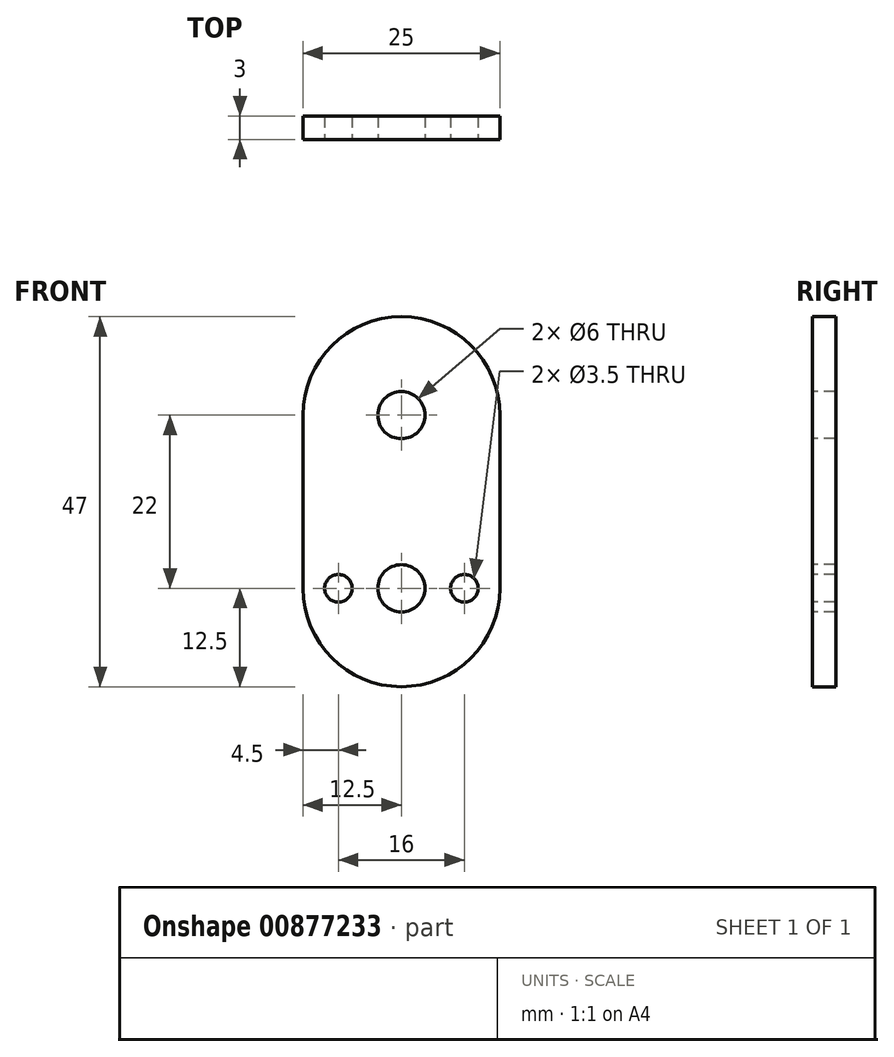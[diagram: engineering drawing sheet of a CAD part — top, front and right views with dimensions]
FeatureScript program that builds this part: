
annotation { "Feature Type Name" : "Feature", "Feature Type Description" : "" }
export const myFeature = defineFeature(function(context is Context, id is Id, definition is map)
    precondition{}
    {
        {
            var Q0;
            Q0=qCreatedBy(makeId("Front.planeOp"),FACE);
            var sketch = newSketch(context, id + "F0", { "sketchPlane" : qUnion([Q0])});
            skCircle(sketch, "E0", {"center": v(0, 11) * mm, "radius": 12.5 * mm});
            skLineSegment(sketch, "E1", {"start": v(-12.5, 11) * mm, "end": v(-12.5, 0) * mm});
            skLineSegment(sketch, "E2", {"start": v(12.5, 11) * mm, "end": v(12.5, 0) * mm});
            skLineSegment(sketch, "E3", {"start": v(12.5, 0) * mm, "end": v(-12.5, 0) * mm});
            skSolve(sketch);
        }
        {
            var Q0;
            {var subQ0=sQuery(id+"F0.wireOp",EDGE,"E0");var subQ1=makeQuery(id+"F0.imprint","INTERSECT",VERTEX,{"derivedFrom":[subQ0,sQuery(id+"F0.wireOp",EDGE,"E1")]});Q0=makeQuery(id+"F0.imprint","IMPRINT",FACE,{"disambiguationData":[TD([[makeQuery(id+"F0.imprint","IMPRINT",EDGE,{"disambiguationData":[TD([[subQ1,1.0]])],"derivedFrom":subQ0}),1.0]])]});}
            var Q1;
            {var subQ0=sQuery(id+"F0.wireOp",EDGE,"E1");Q1=makeQuery(id+"F0.imprint","IMPRINT",FACE,{"disambiguationData":[TD([[makeQuery(id+"F0.imprint","IMPRINT",EDGE,{"derivedFrom":subQ0}),1.0]])]});}
            extrude(context, id + "F1", {"entities" : qUnion([Q0, Q1]), "depth" : 3 * mm, "offsetDistance" : 25 * mm});
        }
        {
            var Q0;
            Q0=makeQuery(id+"F1.opExtrude","CAP_FACE",FACE,{"disambiguationData":[OSD([sQuery(id+"F0.wireOp",EDGE,"E0"),sQuery(id+"F0.wireOp",EDGE,"E1"),sQuery(id+"F0.wireOp",EDGE,"E2"),sQuery(id+"F0.wireOp",EDGE,"E3")])],"isStart":false});
            var sketch = newSketch(context, id + "F2", { "sketchPlane" : qUnion([Q0])});
            skCircle(sketch, "E4", {"center": v(0, 11) * mm, "radius": 3 * mm});
            skSolve(sketch);
        }
        {
            var Q0;
            Q0=makeQuery(id+"F2.imprint","IMPRINT",FACE,{"disambiguationData":[TD([[makeQuery(id+"F2.imprint","IMPRINT",EDGE,{"derivedFrom":sQuery(id+"F2.wireOp",EDGE,"E4")}),1.0]])]});
            extrude(context, id + "F3", {"entities" : qUnion([Q0]), "operationType" : NewBodyOperationType.REMOVE, "oppositeDirection" : true, "depth" : 25 * mm, "offsetDistance" : 25 * mm});
        }
        {
            var Q0;
            Q0=makeQuery(id+"F1.opExtrude","SWEPT_BODY",BODY,{"disambiguationData":[OSD([sQuery(id+"F0.wireOp",EDGE,"E0"),sQuery(id+"F0.wireOp",EDGE,"E1"),sQuery(id+"F0.wireOp",EDGE,"E2"),sQuery(id+"F0.wireOp",EDGE,"E3")])]});
            var Q1;
            Q1=makeQuery(id+"F1.opExtrude","SWEPT_FACE",FACE,{"disambiguationData":[OSD([sQuery(id+"F0.wireOp",EDGE,"E3")])]});
            mirror(context, id + "F4", {"operationType" : NewBodyOperationType.ADD, "entities" : qUnion([Q0]), "mirrorPlane" : qUnion([Q1])});
        }
        {
            var Q0;
            {var subQ0=makeQuery(id+"F1.opExtrude","CAP_FACE",FACE,{"disambiguationData":[OSD([sQuery(id+"F0.wireOp",EDGE,"E0"),sQuery(id+"F0.wireOp",EDGE,"E1"),sQuery(id+"F0.wireOp",EDGE,"E2"),sQuery(id+"F0.wireOp",EDGE,"E3")])],"isStart":false});Q0=makeQuery(id+"F4.boolean.opBoolean","MERGE",FACE,{"derivedFrom":[subQ0,makeQuery(id+"F4.opPattern","COPY",FACE,{"derivedFrom":subQ0,"instanceName":"1"})]});}
            var sketch = newSketch(context, id + "F5", { "sketchPlane" : qUnion([Q0])});
            skCircle(sketch, "E5", {"center": v(0, -11) * mm, "radius": 8 * mm});
            skCircle(sketch, "E6", {"center": v(-8, -11) * mm, "radius": 1.75 * mm});
            skCircle(sketch, "E7", {"center": v(8, -11) * mm, "radius": 1.75 * mm});
            skSolve(sketch);
        }
        {
            var Q0;
            {var subQ0=sQuery(id+"F5.wireOp",EDGE,"E6");var subQ1=sQuery(id+"F5.wireOp",EDGE,"E5");var subQ2=makeQuery(id+"F5.imprint","INTERSECT",VERTEX,{"disambiguationData":[OD(0.0)],"derivedFrom":[subQ1,subQ0]});Q0=makeQuery(id+"F5.imprint","IMPRINT",FACE,{"disambiguationData":[TD([[makeQuery(id+"F5.imprint","IMPRINT",EDGE,{"disambiguationData":[TD([[subQ2,-1.0]])],"derivedFrom":subQ1}),-1.0]])]});}
            var Q1;
            {var subQ0=sQuery(id+"F5.wireOp",EDGE,"E6");var subQ1=sQuery(id+"F5.wireOp",EDGE,"E5");var subQ2=makeQuery(id+"F5.imprint","INTERSECT",VERTEX,{"disambiguationData":[OD(0.0)],"derivedFrom":[subQ1,subQ0]});Q1=makeQuery(id+"F5.imprint","IMPRINT",FACE,{"disambiguationData":[TD([[makeQuery(id+"F5.imprint","IMPRINT",EDGE,{"disambiguationData":[TD([[subQ2,-1.0]])],"derivedFrom":subQ1}),1.0]])]});}
            var Q2;
            {var subQ0=sQuery(id+"F5.wireOp",EDGE,"E7");var subQ1=sQuery(id+"F5.wireOp",EDGE,"E5");var subQ2=makeQuery(id+"F5.imprint","INTERSECT",VERTEX,{"disambiguationData":[OD(0.0)],"derivedFrom":[subQ1,subQ0]});Q2=makeQuery(id+"F5.imprint","IMPRINT",FACE,{"disambiguationData":[TD([[makeQuery(id+"F5.imprint","IMPRINT",EDGE,{"disambiguationData":[TD([[subQ2,1.0]])],"derivedFrom":subQ1}),-1.0]])]});}
            var Q3;
            {var subQ0=sQuery(id+"F5.wireOp",EDGE,"E7");var subQ1=sQuery(id+"F5.wireOp",EDGE,"E5");var subQ2=makeQuery(id+"F5.imprint","INTERSECT",VERTEX,{"disambiguationData":[OD(0.0)],"derivedFrom":[subQ1,subQ0]});Q3=makeQuery(id+"F5.imprint","IMPRINT",FACE,{"disambiguationData":[TD([[makeQuery(id+"F5.imprint","IMPRINT",EDGE,{"disambiguationData":[TD([[subQ2,1.0]])],"derivedFrom":subQ1}),1.0]])]});}
            extrude(context, id + "F6", {"entities" : qUnion([Q0, Q1, Q2, Q3]), "operationType" : NewBodyOperationType.REMOVE, "oppositeDirection" : true, "depth" : 25 * mm, "offsetDistance" : 25 * mm});
        }
        {
            var Q0;
            {var subQ0=makeQuery(id+"F1.opExtrude","CAP_FACE",FACE,{"disambiguationData":[OSD([sQuery(id+"F0.wireOp",EDGE,"E0"),sQuery(id+"F0.wireOp",EDGE,"E1"),sQuery(id+"F0.wireOp",EDGE,"E3")])],"isStart":false});Q0=makeQuery(id+"F4.boolean.opBoolean","MERGE",FACE,{"derivedFrom":[subQ0,makeQuery(id+"F4.opPattern","COPY",FACE,{"derivedFrom":subQ0,"instanceName":"1"})]});}
            var sketch = newSketch(context, id + "F7", { "sketchPlane" : qUnion([Q0])});
            skLineSegment(sketch, "E8", {"start": v(12.5, 11) * mm, "end": v(12.5, -11) * mm});
            skSolve(sketch);
        }
        {
            var Q0;
            Q0 = qSketchRegion(id + "F7", true);
            var Q1;
            {var subQ0=sQuery(id+"F7.wireOp",EDGE,"E8");Q1=makeQuery(id+"F7.imprint","IMPRINT",FACE,{"disambiguationData":[TD([[makeQuery(id+"F7.imprint","IMPRINT",EDGE,{"derivedFrom":subQ0}),-1.0]])]});}
            extrude(context, id + "F8", {"entities" : qUnion([Q0, Q1]), "operationType" : NewBodyOperationType.ADD, "oppositeDirection" : true, "depth" : 3 * mm, "offsetDistance" : 25 * mm});
        }
    });
